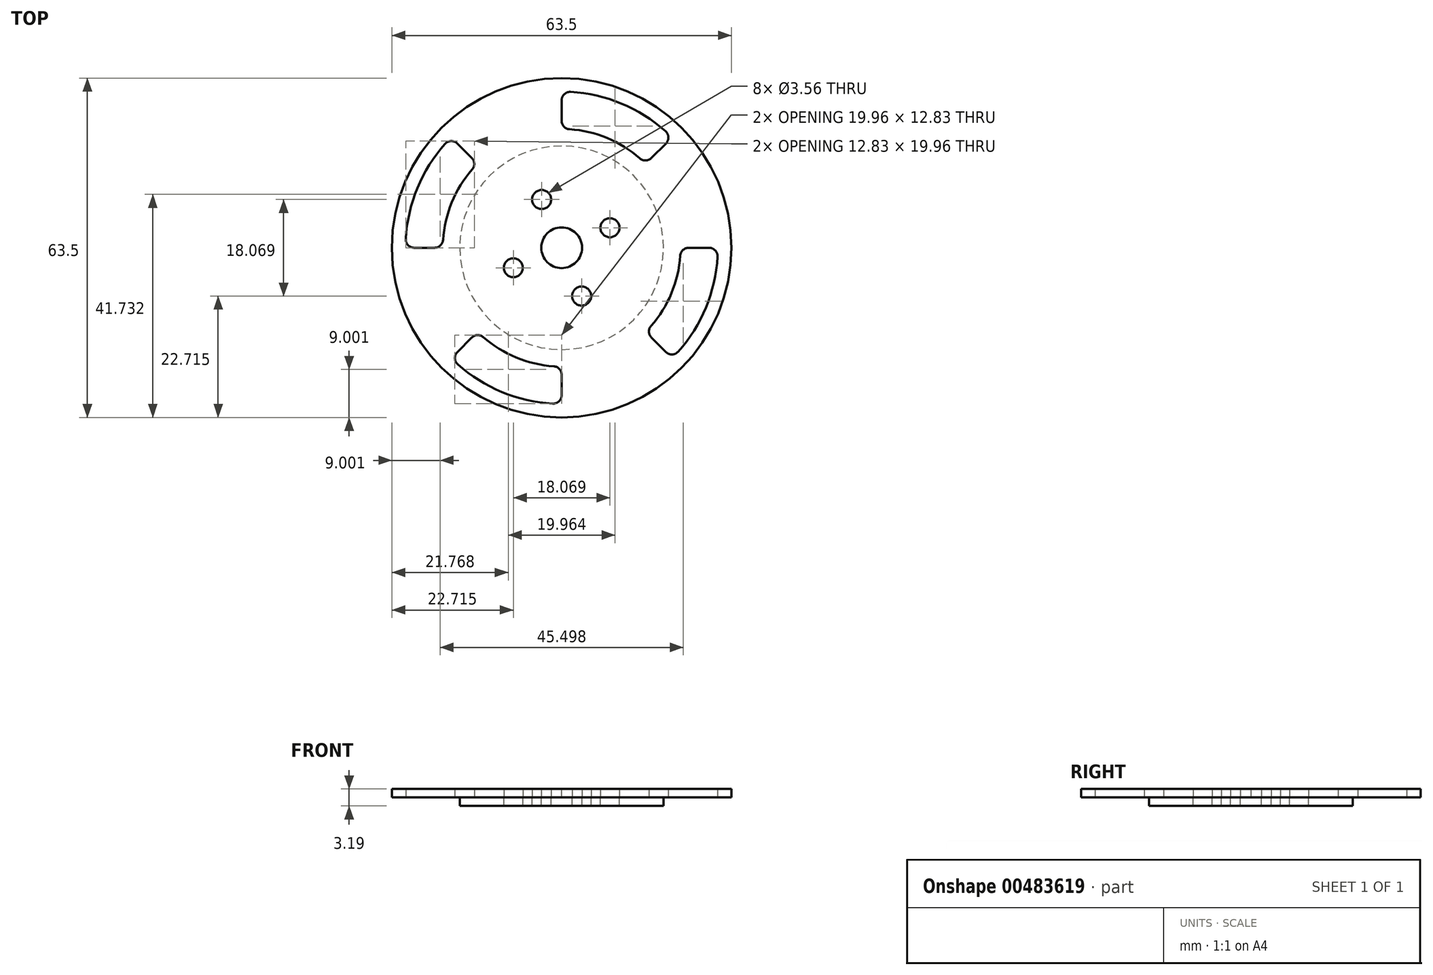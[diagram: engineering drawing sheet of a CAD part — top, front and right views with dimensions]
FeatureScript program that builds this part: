
annotation { "Feature Type Name" : "Feature", "Feature Type Description" : "" }
export const myFeature = defineFeature(function(context is Context, id is Id, definition is map)
    precondition{}
    {
        {
            var Q0;
            Q0=qCreatedBy(makeId("Top.planeOp"),FACE);
            var sketch = newSketch(context, id + "F0", { "sketchPlane" : qUnion([Q0])});
            skCircle(sketch, "E0", {"center": v(0, 0) * mm, "radius": 31.75 * mm});
            skCircle(sketch, "E1", {"center": v(0, 0) * mm, "radius": 29.21 * mm, "construction": true});
            skCircle(sketch, "E2", {"center": v(0, 0) * mm, "radius": 22.22 * mm, "construction": true});
            skLineSegment(sketch, "E3", {"start": v(0, 22.22) * mm, "end": v(0, 29.21) * mm});
            skLineSegment(sketch, "E4", {"start": v(15.72, 15.72) * mm, "end": v(20.65, 20.65) * mm});
            skArc(sketch, "E5", {"start": v(20.65, 20.65) * mm, "mid": v(11.18, 26.99) * mm, "end": v(0, 29.21) * mm});
            skArc(sketch, "E6", {"start": v(15.72, 15.72) * mm, "mid": v(8.5, 20.53) * mm, "end": v(0, 22.22) * mm});
            skLineSegment(sketch, "E7.1.0", {"start": v(-22.22, 0) * mm, "end": v(-29.21, 0) * mm});
            skLineSegment(sketch, "E7.1.1", {"start": v(-15.72, 15.72) * mm, "end": v(-20.65, 20.65) * mm});
            skArc(sketch, "E7.1.2", {"start": v(-20.65, 20.65) * mm, "mid": v(-26.99, 11.18) * mm, "end": v(-29.21, 0) * mm});
            skArc(sketch, "E7.1.3", {"start": v(-15.72, 15.72) * mm, "mid": v(-20.53, 8.5) * mm, "end": v(-22.22, 0) * mm});
            skLineSegment(sketch, "E7.2.0", {"start": v(0, -22.22) * mm, "end": v(0, -29.21) * mm});
            skLineSegment(sketch, "E7.2.1", {"start": v(-15.72, -15.72) * mm, "end": v(-20.65, -20.65) * mm});
            skArc(sketch, "E7.2.2", {"start": v(-20.65, -20.65) * mm, "mid": v(-11.18, -26.99) * mm, "end": v(0, -29.21) * mm});
            skArc(sketch, "E7.2.3", {"start": v(-15.72, -15.72) * mm, "mid": v(-8.5, -20.53) * mm, "end": v(0, -22.22) * mm});
            skLineSegment(sketch, "E7.3.0", {"start": v(22.22, 0) * mm, "end": v(29.21, 0) * mm});
            skLineSegment(sketch, "E7.3.1", {"start": v(15.72, -15.72) * mm, "end": v(20.65, -20.65) * mm});
            skArc(sketch, "E7.3.2", {"start": v(20.65, -20.65) * mm, "mid": v(26.99, -11.18) * mm, "end": v(29.21, 0) * mm});
            skArc(sketch, "E7.3.3", {"start": v(15.72, -15.72) * mm, "mid": v(20.53, -8.5) * mm, "end": v(22.22, 0) * mm});
            skCircle(sketch, "E8", {"center": v(0, 0) * mm, "radius": 3.81 * mm});
            skCircle(sketch, "E9", {"center": v(-3.74, 9.03) * mm, "radius": 1.78 * mm});
            skCircle(sketch, "E10", {"center": v(9.03, 3.74) * mm, "radius": 1.78 * mm});
            skCircle(sketch, "E11", {"center": v(-9.03, -3.74) * mm, "radius": 1.78 * mm});
            skCircle(sketch, "E12", {"center": v(3.74, -9.03) * mm, "radius": 1.78 * mm});
            skLineSegment(sketch, "E13", {"start": v(-3.74, 9.03) * mm, "end": v(3.74, -9.03) * mm, "construction": true});
            skLineSegment(sketch, "E14", {"start": v(-9.03, -3.74) * mm, "end": v(9.03, 3.74) * mm, "construction": true});
            skLineSegment(sketch, "E15", {"start": v(-15.72, 15.72) * mm, "end": v(0, 22.22) * mm, "construction": true});
            skCircle(sketch, "E16", {"center": v(0, 0) * mm, "radius": 19.05 * mm});
            skSolve(sketch);
        }
        {
            var Q0;
            Q0=makeQuery(id+"F0.imprint","IMPRINT",FACE,{"disambiguationData":[TD([[makeQuery(id+"F0.imprint","IMPRINT",EDGE,{"derivedFrom":sQuery(id+"F0.wireOp",EDGE,"E0")}),1.0]])]});
            var Q1;
            Q1=makeQuery(id+"F0.imprint","IMPRINT",FACE,{"disambiguationData":[TD([[makeQuery(id+"F0.imprint","IMPRINT",EDGE,{"derivedFrom":sQuery(id+"F0.wireOp",EDGE,"E8")}),-1.0]])]});
            extrude(context, id + "F1", {"entities" : qUnion([Q0, Q1]), "depth" : 1.6 * mm});
        }
        {
            var Q0;
            Q0=makeQuery(id+"F1.opExtrude","SWEPT_EDGE",EDGE,{"disambiguationData":[OSD([sQuery(id+"F0.wireOp",EDGE,"E7.1.1"),sQuery(id+"F0.wireOp",EDGE,"E7.1.2")])]});
            var Q1;
            Q1=makeQuery(id+"F1.opExtrude","SWEPT_EDGE",EDGE,{"disambiguationData":[OSD([sQuery(id+"F0.wireOp",EDGE,"E3"),sQuery(id+"F0.wireOp",EDGE,"E5")])]});
            var Q2;
            Q2=makeQuery(id+"F1.opExtrude","SWEPT_EDGE",EDGE,{"disambiguationData":[OSD([sQuery(id+"F0.wireOp",EDGE,"E7.3.0"),sQuery(id+"F0.wireOp",EDGE,"E7.3.3")])]});
            var Q3;
            Q3=makeQuery(id+"F1.opExtrude","SWEPT_EDGE",EDGE,{"disambiguationData":[OSD([sQuery(id+"F0.wireOp",EDGE,"E7.2.1"),sQuery(id+"F0.wireOp",EDGE,"E7.2.3")])]});
            var Q4;
            Q4=makeQuery(id+"F1.opExtrude","SWEPT_EDGE",EDGE,{"disambiguationData":[OSD([sQuery(id+"F0.wireOp",EDGE,"E7.1.0"),sQuery(id+"F0.wireOp",EDGE,"E7.1.2")])]});
            var Q5;
            Q5=makeQuery(id+"F1.opExtrude","SWEPT_EDGE",EDGE,{"disambiguationData":[OSD([sQuery(id+"F0.wireOp",EDGE,"E7.2.1"),sQuery(id+"F0.wireOp",EDGE,"E7.2.2")])]});
            var Q6;
            Q6=makeQuery(id+"F1.opExtrude","SWEPT_EDGE",EDGE,{"disambiguationData":[OSD([sQuery(id+"F0.wireOp",EDGE,"E7.3.1"),sQuery(id+"F0.wireOp",EDGE,"E7.3.3")])]});
            var Q7;
            Q7=makeQuery(id+"F1.opExtrude","SWEPT_EDGE",EDGE,{"disambiguationData":[OSD([sQuery(id+"F0.wireOp",EDGE,"E3"),sQuery(id+"F0.wireOp",EDGE,"E6")])]});
            var Q8;
            Q8=makeQuery(id+"F1.opExtrude","SWEPT_EDGE",EDGE,{"disambiguationData":[OSD([sQuery(id+"F0.wireOp",EDGE,"E4"),sQuery(id+"F0.wireOp",EDGE,"E6")])]});
            var Q9;
            Q9=makeQuery(id+"F1.opExtrude","SWEPT_EDGE",EDGE,{"disambiguationData":[OSD([sQuery(id+"F0.wireOp",EDGE,"E7.3.1"),sQuery(id+"F0.wireOp",EDGE,"E7.3.2")])]});
            var Q10;
            Q10=makeQuery(id+"F1.opExtrude","SWEPT_EDGE",EDGE,{"disambiguationData":[OSD([sQuery(id+"F0.wireOp",EDGE,"E7.2.0"),sQuery(id+"F0.wireOp",EDGE,"E7.2.2")])]});
            var Q11;
            Q11=makeQuery(id+"F1.opExtrude","SWEPT_EDGE",EDGE,{"disambiguationData":[OSD([sQuery(id+"F0.wireOp",EDGE,"E7.1.0"),sQuery(id+"F0.wireOp",EDGE,"E7.1.3")])]});
            var Q12;
            Q12=makeQuery(id+"F1.opExtrude","SWEPT_EDGE",EDGE,{"disambiguationData":[OSD([sQuery(id+"F0.wireOp",EDGE,"E4"),sQuery(id+"F0.wireOp",EDGE,"E5")])]});
            var Q13;
            Q13=makeQuery(id+"F1.opExtrude","SWEPT_EDGE",EDGE,{"disambiguationData":[OSD([sQuery(id+"F0.wireOp",EDGE,"E7.3.0"),sQuery(id+"F0.wireOp",EDGE,"E7.3.2")])]});
            var Q14;
            Q14=makeQuery(id+"F1.opExtrude","SWEPT_EDGE",EDGE,{"disambiguationData":[OSD([sQuery(id+"F0.wireOp",EDGE,"E7.2.0"),sQuery(id+"F0.wireOp",EDGE,"E7.2.3")])]});
            var Q15;
            Q15=makeQuery(id+"F1.opExtrude","SWEPT_EDGE",EDGE,{"disambiguationData":[OSD([sQuery(id+"F0.wireOp",EDGE,"E7.1.1"),sQuery(id+"F0.wireOp",EDGE,"E7.1.3")])]});
            fillet(context, id + "F2", {"entities" : qUnion([Q0, Q1, Q2, Q3, Q4, Q5, Q6, Q7, Q8, Q9, Q10, Q11, Q12, Q13, Q14, Q15]), "radius" : 1.59 * mm, "tangentPropagation" : true, "allowEdgeOverflow" : false});
        }
        {
            var Q0;
            Q0=makeQuery(id+"F0.imprint","IMPRINT",FACE,{"disambiguationData":[TD([[makeQuery(id+"F0.imprint","IMPRINT",EDGE,{"derivedFrom":sQuery(id+"F0.wireOp",EDGE,"E8")}),-1.0]])]});
            extrude(context, id + "F3", {"entities" : qUnion([Q0]), "oppositeDirection" : true, "depth" : 1.59 * mm});
        }
    });
